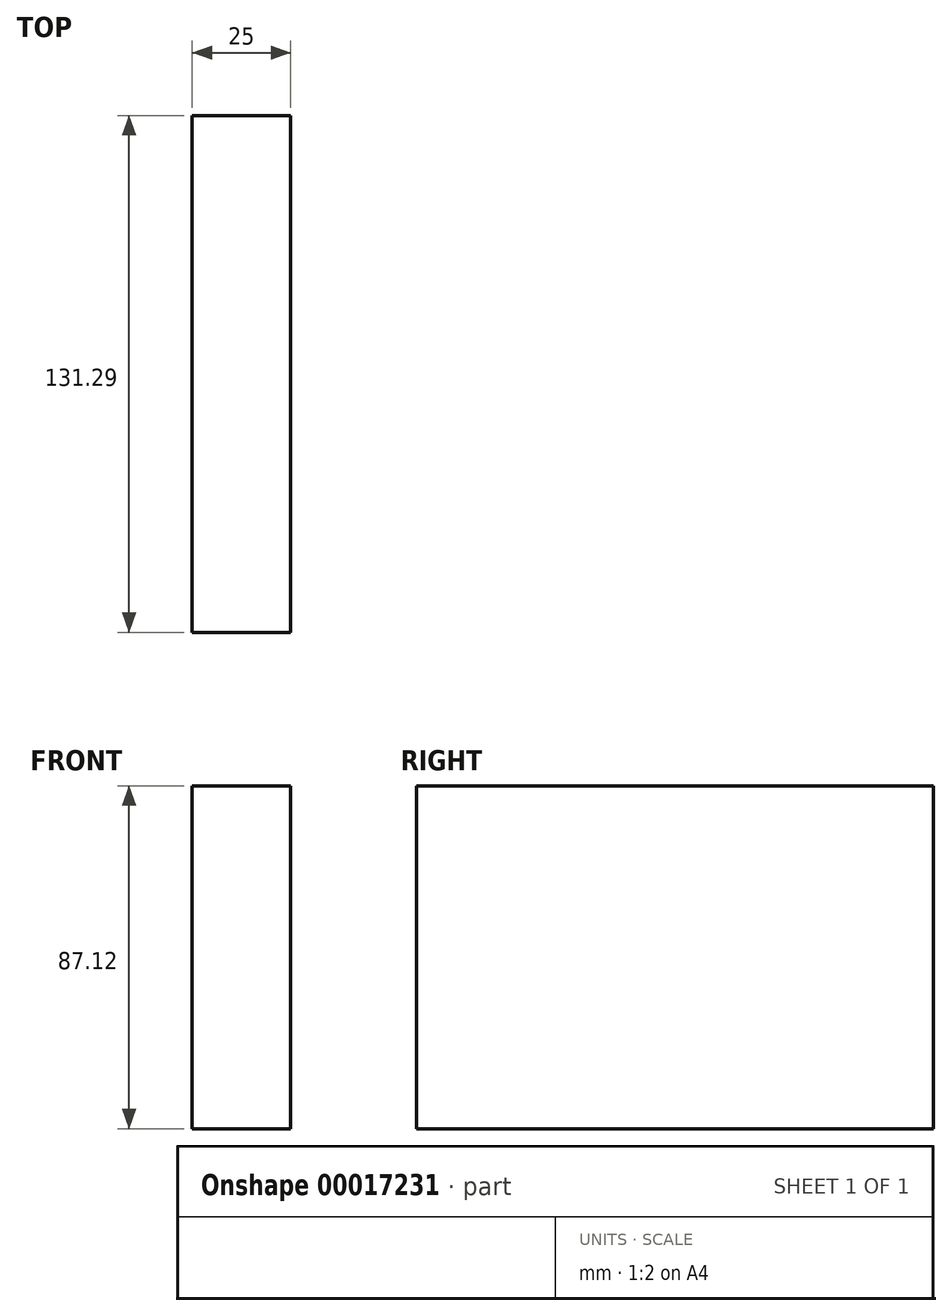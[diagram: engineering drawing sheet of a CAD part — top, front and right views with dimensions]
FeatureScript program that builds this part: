
annotation { "Feature Type Name" : "Feature", "Feature Type Description" : "" }
export const myFeature = defineFeature(function(context is Context, id is Id, definition is map)
    precondition{}
    {
        {
            var Q0;
            Q0=qCreatedBy(makeId("Right.planeOp"),FACE);
            var sketch = newSketch(context, id + "F0", { "sketchPlane" : qUnion([Q0])});
            skLineSegment(sketch, "E0.bottom", {"start": v(-45.22, 35.45) * mm, "end": v(86.07, 35.45) * mm});
            skLineSegment(sketch, "E0.top", {"start": v(-45.22, -51.67) * mm, "end": v(86.07, -51.67) * mm});
            skLineSegment(sketch, "E0.left", {"start": v(-45.22, 35.45) * mm, "end": v(-45.22, -51.67) * mm});
            skLineSegment(sketch, "E0.right", {"start": v(86.07, 35.45) * mm, "end": v(86.07, -51.67) * mm});
            skSolve(sketch);
        }
        {
            var Q0;
            Q0 = qSketchRegion(id + "F0", true);
            extrude(context, id + "F1", {"entities" : qUnion([Q0]), "depth" : 25 * mm});
        }
    });
